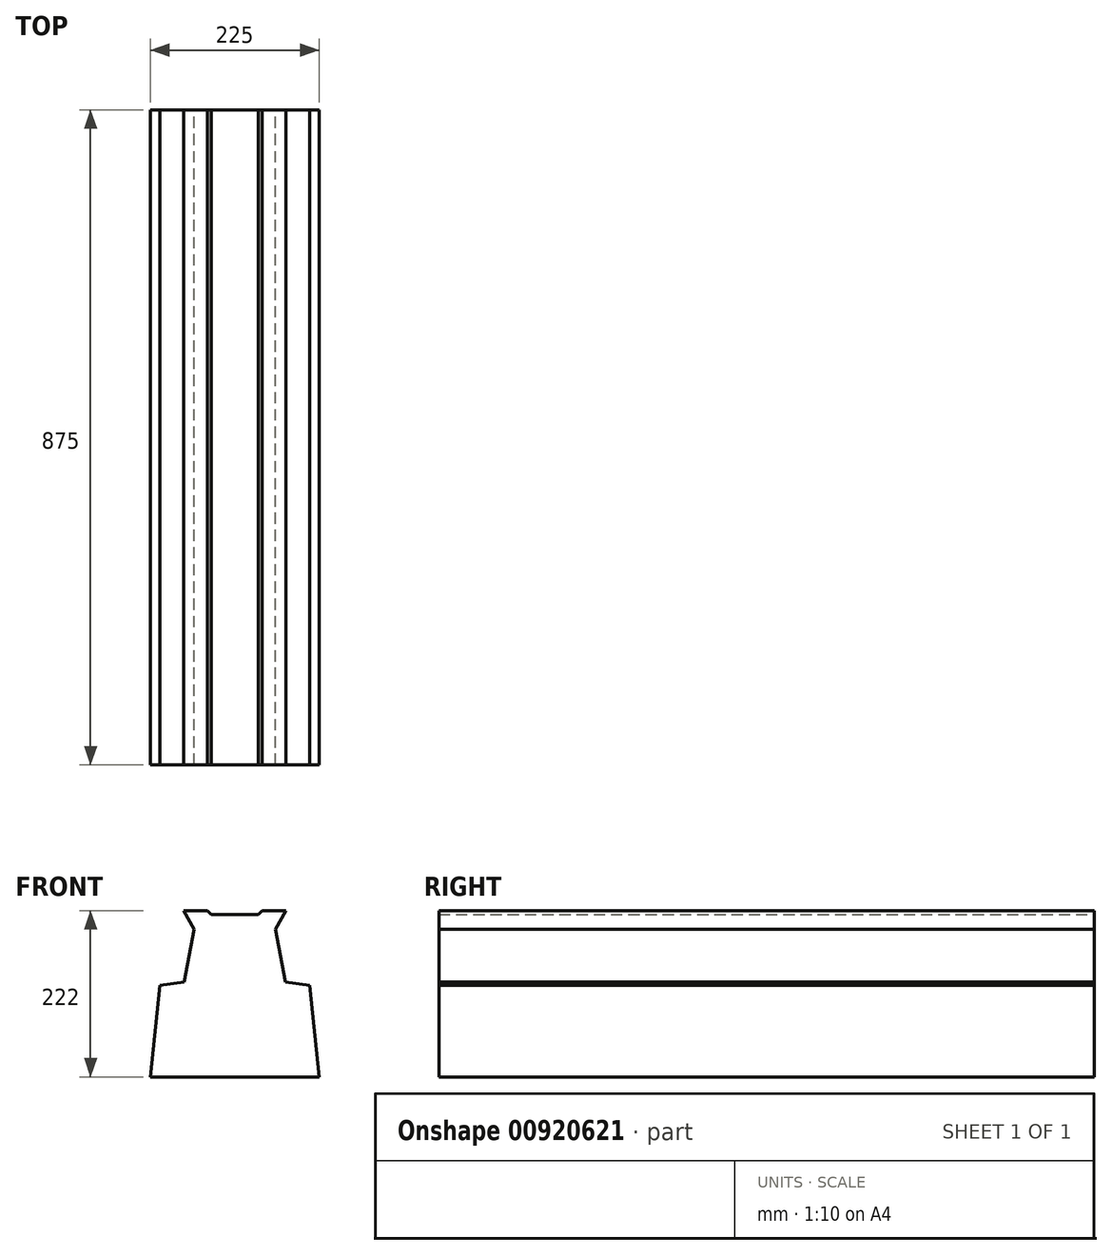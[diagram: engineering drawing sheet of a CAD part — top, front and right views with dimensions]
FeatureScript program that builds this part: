
annotation { "Feature Type Name" : "Feature", "Feature Type Description" : "" }
export const myFeature = defineFeature(function(context is Context, id is Id, definition is map)
    precondition{}
    {
        {
            var Q0;
            Q0=qCreatedBy(makeId("Front.planeOp"),FACE);
            var sketch = newSketch(context, id + "F0", { "sketchPlane" : qUnion([Q0])});
            skLineSegment(sketch, "E0", {"start": v(-68.5, 0) * mm, "end": v(-36.25, 0) * mm});
            skLineSegment(sketch, "E1", {"start": v(-36.25, 0) * mm, "end": v(-31.25, -5) * mm});
            skLineSegment(sketch, "E2", {"start": v(-31.25, -5) * mm, "end": v(31.25, -5) * mm});
            skLineSegment(sketch, "E3", {"start": v(31.25, -5) * mm, "end": v(36.25, 0) * mm});
            skLineSegment(sketch, "E4", {"start": v(36.25, 0) * mm, "end": v(68.5, 0) * mm});
            skLineSegment(sketch, "E5", {"start": v(-68.5, 0) * mm, "end": v(-54.07, -25) * mm});
            skLineSegment(sketch, "E6", {"start": v(-54.07, -25) * mm, "end": v(-67.5, -95) * mm});
            skLineSegment(sketch, "E7", {"start": v(-67.5, -95) * mm, "end": v(-100, -100) * mm});
            skLineSegment(sketch, "E8", {"start": v(-100, -100) * mm, "end": v(-112.5, -222) * mm});
            skLineSegment(sketch, "E9", {"start": v(-112.5, -222) * mm, "end": v(112.5, -222) * mm});
            skLineSegment(sketch, "E10", {"start": v(68.5, 0) * mm, "end": v(54.07, -25) * mm});
            skLineSegment(sketch, "E11", {"start": v(54.07, -25) * mm, "end": v(67.5, -95) * mm});
            skLineSegment(sketch, "E12", {"start": v(67.5, -95) * mm, "end": v(100, -100) * mm});
            skLineSegment(sketch, "E13", {"start": v(100, -100) * mm, "end": v(112.5, -222) * mm});
            skSolve(sketch);
        }
        {
            var Q0;
            Q0=makeQuery(id+"F0.imprint","IMPRINT",FACE,{"disambiguationData":[TD([[makeQuery(id+"F0.imprint","IMPRINT",EDGE,{"derivedFrom":sQuery(id+"F0.wireOp",EDGE,"E0")}),-1.0]])]});
            extrude(context, id + "F1", {"entities" : qUnion([Q0]), "depth" : 875 * mm, "offsetDistance" : 25 * mm});
        }
    });
